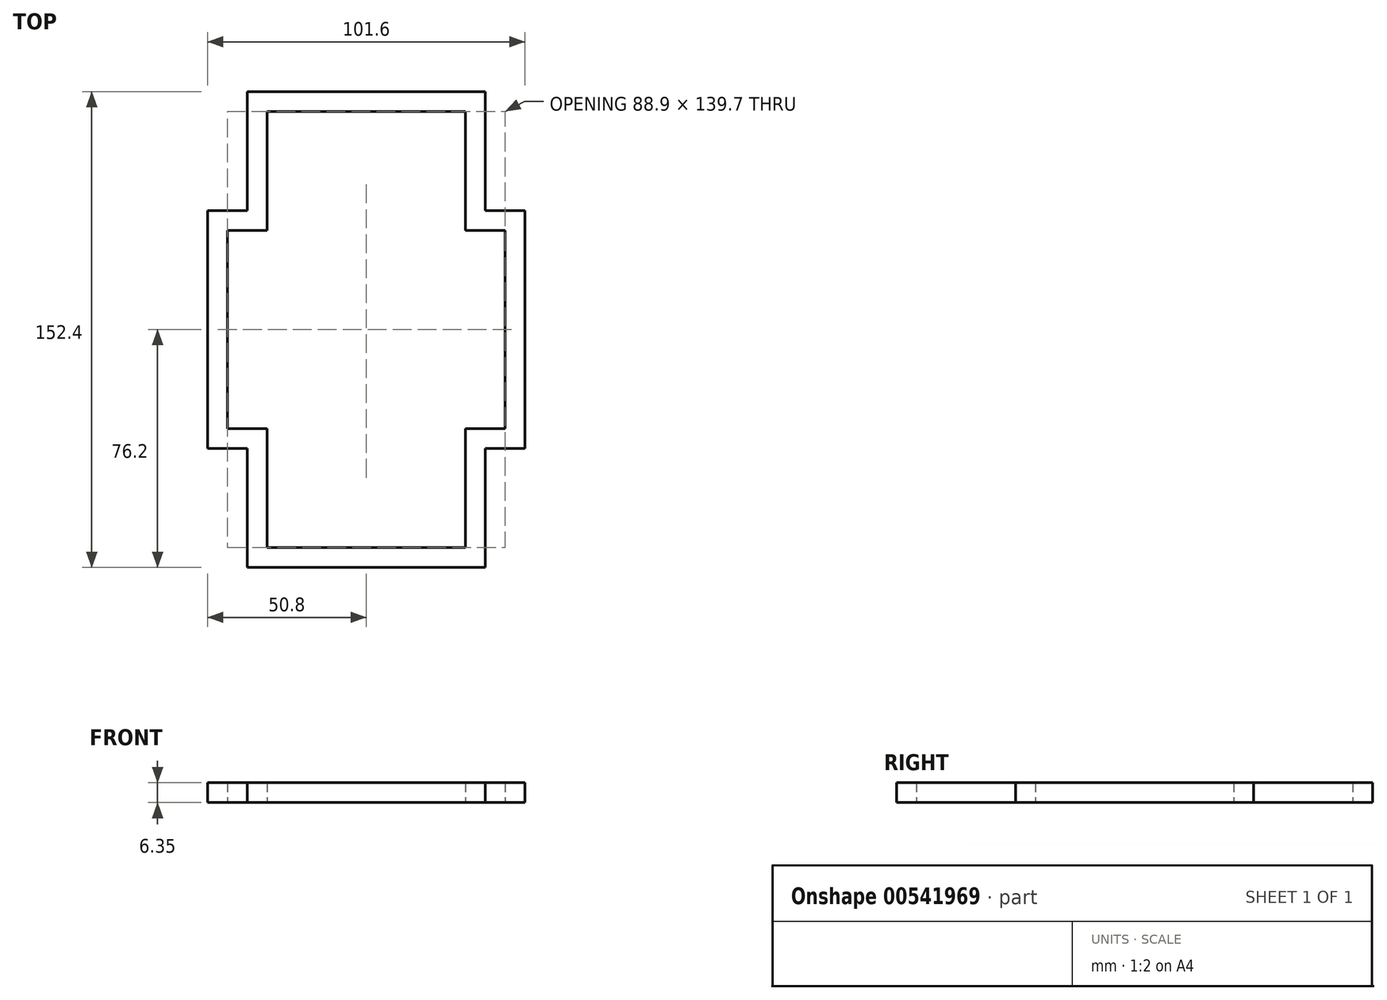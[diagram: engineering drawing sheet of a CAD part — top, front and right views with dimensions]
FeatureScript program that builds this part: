
annotation { "Feature Type Name" : "Feature", "Feature Type Description" : "" }
export const myFeature = defineFeature(function(context is Context, id is Id, definition is map)
    precondition{}
    {
        {
            var Q0;
            Q0=qCreatedBy(makeId("Top.planeOp"),FACE);
            var sketch = newSketch(context, id + "F0", { "sketchPlane" : qUnion([Q0])});
            skLineSegment(sketch, "E0", {"start": v(-50.8, 76.2) * mm, "end": v(0, 76.2) * mm, "construction": true});
            skLineSegment(sketch, "E1", {"start": v(0, 76.2) * mm, "end": v(50.8, 76.2) * mm, "construction": true});
            skLineSegment(sketch, "E2", {"start": v(50.8, 76.2) * mm, "end": v(50.8, 0) * mm, "construction": true});
            skLineSegment(sketch, "E3", {"start": v(50.8, 0) * mm, "end": v(50.8, -76.2) * mm, "construction": true});
            skLineSegment(sketch, "E4", {"start": v(50.8, -76.2) * mm, "end": v(0, -76.2) * mm, "construction": true});
            skLineSegment(sketch, "E5", {"start": v(0, -76.2) * mm, "end": v(-50.8, -76.2) * mm, "construction": true});
            skLineSegment(sketch, "E6", {"start": v(-50.8, -76.2) * mm, "end": v(-50.8, 0) * mm, "construction": true});
            skLineSegment(sketch, "E7", {"start": v(-50.8, 0) * mm, "end": v(-50.8, 76.2) * mm, "construction": true});
            skLineSegment(sketch, "E8", {"start": v(50.8, 38.1) * mm, "end": v(-50.8, 38.1) * mm, "construction": true});
            skLineSegment(sketch, "E9", {"start": v(50.8, -38.1) * mm, "end": v(-50.8, -38.1) * mm, "construction": true});
            skLineSegment(sketch, "E10", {"start": v(-38.1, -76.2) * mm, "end": v(-38.1, 76.2) * mm, "construction": true});
            skLineSegment(sketch, "E11", {"start": v(38.1, -76.2) * mm, "end": v(38.1, 76.2) * mm, "construction": true});
            skLineSegment(sketch, "E12", {"start": v(38.1, 76.2) * mm, "end": v(-38.1, 76.2) * mm});
            skLineSegment(sketch, "E13", {"start": v(-38.1, 76.2) * mm, "end": v(-38.1, 38.1) * mm});
            skLineSegment(sketch, "E14", {"start": v(-38.1, 38.1) * mm, "end": v(-50.8, 38.1) * mm});
            skLineSegment(sketch, "E15", {"start": v(-50.8, 38.1) * mm, "end": v(-50.8, -38.1) * mm});
            skLineSegment(sketch, "E16", {"start": v(-50.8, -38.1) * mm, "end": v(-38.1, -38.1) * mm});
            skLineSegment(sketch, "E17", {"start": v(-38.1, -38.1) * mm, "end": v(-38.1, -76.2) * mm});
            skLineSegment(sketch, "E18", {"start": v(-38.1, -76.2) * mm, "end": v(38.1, -76.2) * mm});
            skLineSegment(sketch, "E19", {"start": v(38.1, -76.2) * mm, "end": v(38.1, -38.1) * mm});
            skLineSegment(sketch, "E20", {"start": v(38.1, -38.1) * mm, "end": v(50.8, -38.1) * mm});
            skLineSegment(sketch, "E21", {"start": v(50.8, -38.1) * mm, "end": v(50.8, 38.1) * mm});
            skLineSegment(sketch, "E22", {"start": v(50.8, 38.1) * mm, "end": v(38.1, 38.1) * mm});
            skLineSegment(sketch, "E23", {"start": v(38.1, 38.1) * mm, "end": v(38.1, 76.2) * mm});
            skSolve(sketch);
        }
        {
            var Q0;
            Q0 = qSketchRegion(id + "F0", true);
            extrude(context, id + "F1", {"entities" : qUnion([Q0]), "depth" : 6.35 * mm, "offsetDistance" : 25.4 * mm});
        }
        {
            var Q0;
            Q0=makeQuery(id+"F1.opExtrude","CAP_FACE",FACE,{"disambiguationData":[OSD([sQuery(id+"F0.wireOp",EDGE,"E12"),sQuery(id+"F0.wireOp",EDGE,"E13"),sQuery(id+"F0.wireOp",EDGE,"E14"),sQuery(id+"F0.wireOp",EDGE,"E15"),sQuery(id+"F0.wireOp",EDGE,"E16"),sQuery(id+"F0.wireOp",EDGE,"E17"),sQuery(id+"F0.wireOp",EDGE,"E18"),sQuery(id+"F0.wireOp",EDGE,"E19"),sQuery(id+"F0.wireOp",EDGE,"E20"),sQuery(id+"F0.wireOp",EDGE,"E21"),sQuery(id+"F0.wireOp",EDGE,"E22"),sQuery(id+"F0.wireOp",EDGE,"E23")])],"isStart":false});
            var Q1;
            Q1=makeQuery(id+"F1.opExtrude","CAP_FACE",FACE,{"disambiguationData":[OSD([sQuery(id+"F0.wireOp",EDGE,"E12"),sQuery(id+"F0.wireOp",EDGE,"E13"),sQuery(id+"F0.wireOp",EDGE,"E14"),sQuery(id+"F0.wireOp",EDGE,"E15"),sQuery(id+"F0.wireOp",EDGE,"E16"),sQuery(id+"F0.wireOp",EDGE,"E17"),sQuery(id+"F0.wireOp",EDGE,"E18"),sQuery(id+"F0.wireOp",EDGE,"E19"),sQuery(id+"F0.wireOp",EDGE,"E20"),sQuery(id+"F0.wireOp",EDGE,"E21"),sQuery(id+"F0.wireOp",EDGE,"E22"),sQuery(id+"F0.wireOp",EDGE,"E23")])],"isStart":true});
            var Q2;
            Q2=makeQuery(id+"F1.opExtrude","SWEPT_BODY",BODY,{"disambiguationData":[OSD([sQuery(id+"F0.wireOp",EDGE,"E12"),sQuery(id+"F0.wireOp",EDGE,"E13"),sQuery(id+"F0.wireOp",EDGE,"E14"),sQuery(id+"F0.wireOp",EDGE,"E15"),sQuery(id+"F0.wireOp",EDGE,"E16"),sQuery(id+"F0.wireOp",EDGE,"E17"),sQuery(id+"F0.wireOp",EDGE,"E18"),sQuery(id+"F0.wireOp",EDGE,"E19"),sQuery(id+"F0.wireOp",EDGE,"E20"),sQuery(id+"F0.wireOp",EDGE,"E21"),sQuery(id+"F0.wireOp",EDGE,"E22"),sQuery(id+"F0.wireOp",EDGE,"E23")])]});
            shell(context, id + "F2", {"entities" : qUnion([Q0, Q1]), "parts" : qUnion([Q2]), "thickness" : 6.35 * mm});
        }
    });
